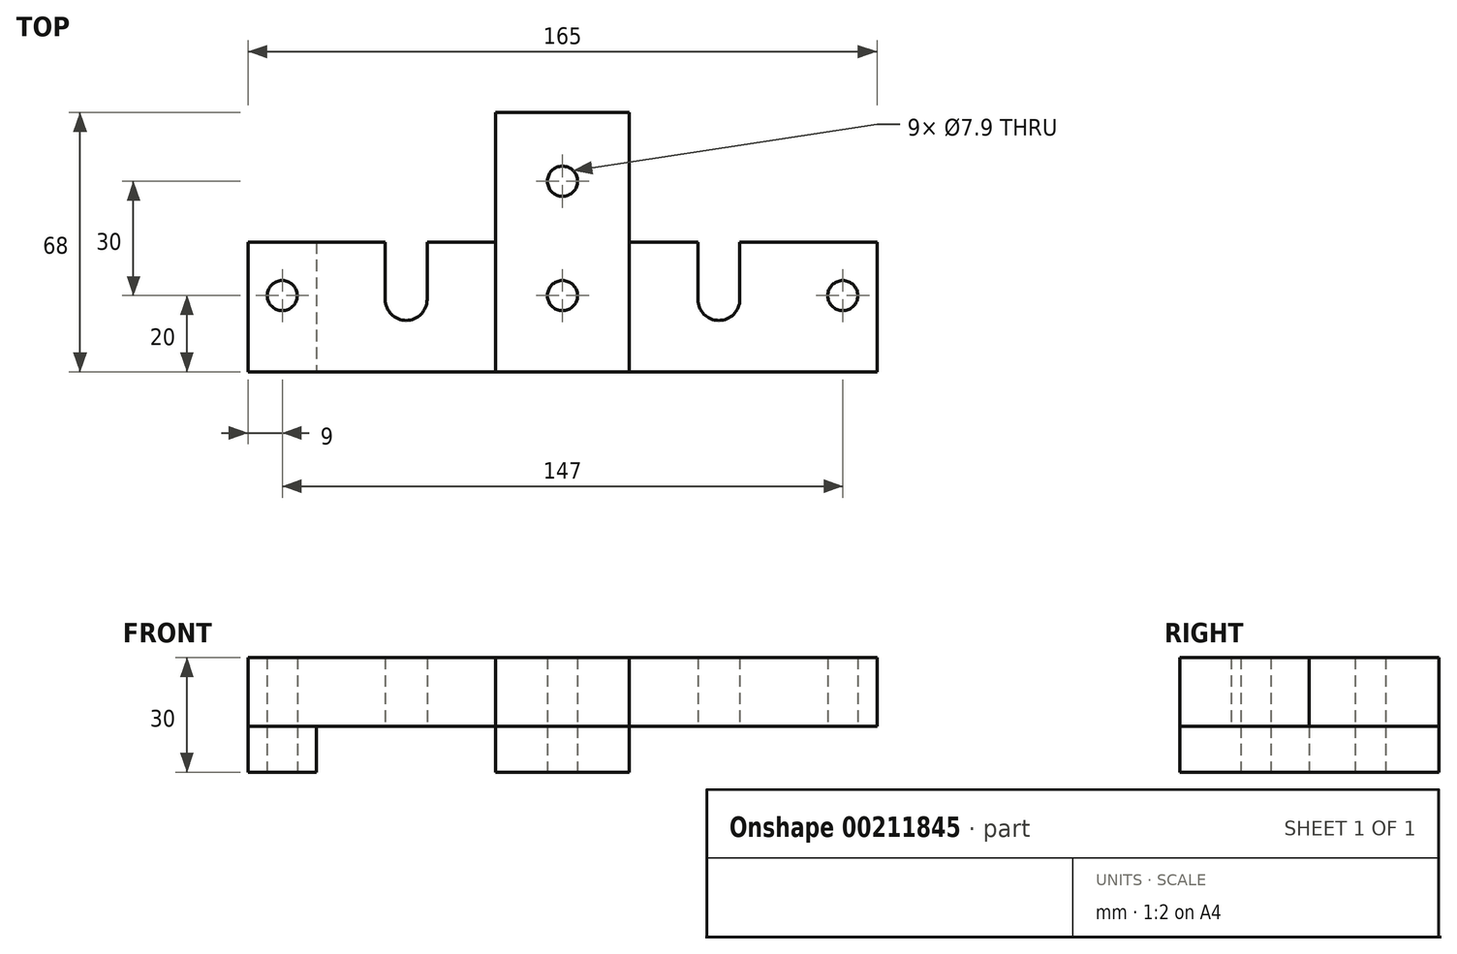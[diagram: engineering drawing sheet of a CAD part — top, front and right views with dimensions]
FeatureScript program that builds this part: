
annotation { "Feature Type Name" : "Feature", "Feature Type Description" : "" }
export const myFeature = defineFeature(function(context is Context, id is Id, definition is map)
    precondition{}
    {
        {
            var Q0;
            Q0=qCreatedBy(makeId("Top.planeOp"),FACE);
            var sketch = newSketch(context, id + "F0", { "sketchPlane" : qUnion([Q0])});
            skLineSegment(sketch, "E0.bottom", {"start": v(-17.5, 33) * mm, "end": v(17.5, 33) * mm});
            skLineSegment(sketch, "E0.top", {"start": v(-17.5, -35) * mm, "end": v(17.5, -35) * mm});
            skLineSegment(sketch, "E0.left", {"start": v(-17.5, 33) * mm, "end": v(-17.5, -35) * mm});
            skLineSegment(sketch, "E0.right", {"start": v(17.5, 33) * mm, "end": v(17.5, -35) * mm});
            skCircle(sketch, "E1", {"center": v(0, 15) * mm, "radius": 3.95 * mm});
            skCircle(sketch, "E2", {"center": v(0, -15) * mm, "radius": 3.95 * mm});
            skLineSegment(sketch, "E3", {"start": v(-17.5, -35) * mm, "end": v(-82.5, -35) * mm});
            skLineSegment(sketch, "E4", {"start": v(-82.5, -35) * mm, "end": v(-82.5, -1) * mm});
            skLineSegment(sketch, "E5", {"start": v(-82.5, -1) * mm, "end": v(-64.5, -1) * mm});
            skLineSegment(sketch, "E6", {"start": v(-64.5, -1) * mm, "end": v(-64.5, -35) * mm});
            skLineSegment(sketch, "E7", {"start": v(-64.5, -1) * mm, "end": v(-46.5, -1) * mm});
            skLineSegment(sketch, "E8", {"start": v(-46.5, -1) * mm, "end": v(-46.5, -16) * mm});
            skLineSegment(sketch, "E9", {"start": v(-35.5, -1) * mm, "end": v(-35.5, -16) * mm});
            skArc(sketch, "E10", {"start": v(-46.5, -16) * mm, "mid": v(-41, -21.5) * mm, "end": v(-35.5, -16) * mm});
            skLineSegment(sketch, "E11", {"start": v(-46.5, -16) * mm, "end": v(-64.5, -16) * mm, "construction": true});
            skLineSegment(sketch, "E12", {"start": v(-35.5, -16) * mm, "end": v(-17.5, -16) * mm, "construction": true});
            skLineSegment(sketch, "E13.trimOffspring", {"start": v(-35.5, -1) * mm, "end": v(-17.5, -1) * mm});
            skCircle(sketch, "E14", {"center": v(-73.5, -15) * mm, "radius": 3.95 * mm});
            skLineSegment(sketch, "E15", {"start": v(-73.5, -15) * mm, "end": v(-82.5, -15) * mm, "construction": true});
            skLineSegment(sketch, "E16", {"start": v(-73.5, -15) * mm, "end": v(-64.5, -15) * mm, "construction": true});
            skLineSegment(sketch, "E17", {"start": v(0, 33) * mm, "end": v(0, -35) * mm, "construction": true});
            skSolve(sketch);
        }
        {
            var Q0;
            {var subQ0=sQuery(id+"F0.wireOp",EDGE,"E4");Q0=makeQuery(id+"F0.imprint","IMPRINT",FACE,{"disambiguationData":[TD([[makeQuery(id+"F0.imprint","IMPRINT",EDGE,{"derivedFrom":subQ0}),-1.0]])]});}
            var Q1;
            {var subQ3=sQuery(id+"F0.wireOp",EDGE,"E0.bottom");Q1=makeQuery(id+"F0.imprint","IMPRINT",FACE,{"disambiguationData":[TD([[makeQuery(id+"F0.imprint","IMPRINT",EDGE,{"derivedFrom":subQ3}),-1.0]])]});}
            extrude(context, id + "F1", {"entities" : qUnion([Q0, Q1]), "depth" : 12 * mm, "offsetDistance" : 25 * mm});
        }
        {
            var Q0;
            {var subQ1=sQuery(id+"F0.wireOp",EDGE,"E4");Q0=makeQuery(id+"F0.imprint","IMPRINT",FACE,{"disambiguationData":[TD([[makeQuery(id+"F0.imprint","IMPRINT",EDGE,{"derivedFrom":subQ1}),-1.0]])]});}
            var Q1;
            {var subQ0=sQuery(id+"F0.wireOp",EDGE,"E6");Q1=makeQuery(id+"F0.imprint","IMPRINT",FACE,{"disambiguationData":[TD([[makeQuery(id+"F0.imprint","IMPRINT",EDGE,{"derivedFrom":subQ0}),1.0]])]});}
            var Q2;
            {var subQ3=sQuery(id+"F0.wireOp",EDGE,"E0.bottom");Q2=makeQuery(id+"F0.imprint","IMPRINT",FACE,{"disambiguationData":[TD([[makeQuery(id+"F0.imprint","IMPRINT",EDGE,{"derivedFrom":subQ3}),-1.0]])]});}
            extrude(context, id + "F2", {"entities" : qUnion([Q0, Q1, Q2]), "depth" : 30 * mm, "offsetDistance" : 25 * mm, "hasSecondDirection" : true, "secondDirectionOppositeDirection" : false, "secondDirectionDepth" : 12 * mm});
        }
        {
            var Q0;
            Q0=makeQuery(id+"F2.opExtrude","SWEPT_BODY",BODY,{"disambiguationData":[OSD([sQuery(id+"F0.wireOp",EDGE,"E0.bottom"),sQuery(id+"F0.wireOp",EDGE,"E0.top"),sQuery(id+"F0.wireOp",EDGE,"E0.left"),sQuery(id+"F0.wireOp",EDGE,"E0.right"),sQuery(id+"F0.wireOp",EDGE,"E1"),sQuery(id+"F0.wireOp",EDGE,"E2"),sQuery(id+"F0.wireOp",EDGE,"E3"),sQuery(id+"F0.wireOp",EDGE,"E4"),sQuery(id+"F0.wireOp",EDGE,"E5"),sQuery(id+"F0.wireOp",EDGE,"E7"),sQuery(id+"F0.wireOp",EDGE,"E8"),sQuery(id+"F0.wireOp",EDGE,"E9"),sQuery(id+"F0.wireOp",EDGE,"E10"),sQuery(id+"F0.wireOp",EDGE,"E13.trimOffspring"),sQuery(id+"F0.wireOp",EDGE,"E14")])]});
            var Q1;
            Q1=qCreatedBy(makeId("Right.planeOp"),FACE);
            mirror(context, id + "F3", {"entities" : qUnion([Q0]), "mirrorPlane" : qUnion([Q1])});
        }
    });
